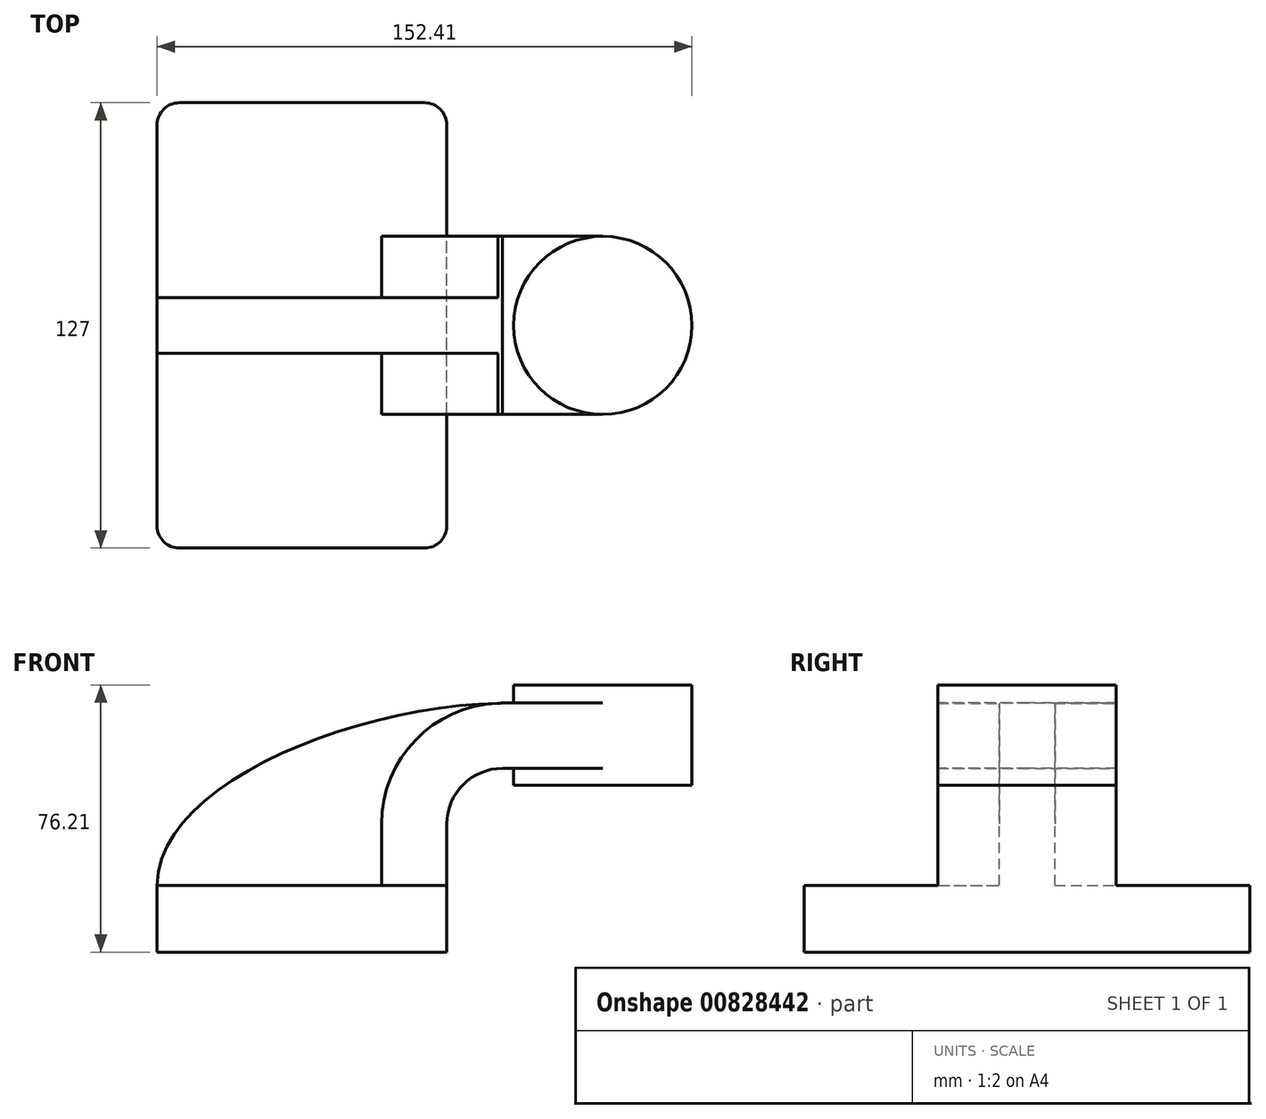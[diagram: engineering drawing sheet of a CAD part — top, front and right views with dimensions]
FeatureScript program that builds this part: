
annotation { "Feature Type Name" : "Feature", "Feature Type Description" : "" }
export const myFeature = defineFeature(function(context is Context, id is Id, definition is map)
    precondition{}
    {
        {
            var Q0;
            Q0=qCreatedBy(makeId("Front.planeOp"),FACE);
            var sketch = newSketch(context, id + "F0", { "sketchPlane" : qUnion([Q0])});
            skLineSegment(sketch, "E0.bottom", {"start": v(-41.28, 9.52) * mm, "end": v(41.28, 9.53) * mm});
            skLineSegment(sketch, "E0.top", {"start": v(-41.28, -9.53) * mm, "end": v(41.28, -9.53) * mm});
            skLineSegment(sketch, "E0.left", {"start": v(-41.28, 9.52) * mm, "end": v(-41.28, -9.53) * mm});
            skLineSegment(sketch, "E0.right", {"start": v(41.28, 9.53) * mm, "end": v(41.28, -9.52) * mm});
            skPoint(sketch, "E0.middle", {"position": v(0, 0) * mm});
            skLineSegment(sketch, "E1.bottom", {"start": v(60.32, 66.67) * mm, "end": v(111.13, 66.67) * mm});
            skLineSegment(sketch, "E1.top", {"start": v(60.32, 38.1) * mm, "end": v(111.13, 38.1) * mm});
            skLineSegment(sketch, "E1.left", {"start": v(60.32, 66.67) * mm, "end": v(60.32, 38.1) * mm});
            skLineSegment(sketch, "E1.right", {"start": v(111.13, 66.67) * mm, "end": v(111.13, 38.1) * mm});
            skPoint(sketch, "E1.middle", {"position": v(85.72, 52.39) * mm});
            skLineSegment(sketch, "E2", {"start": v(41.27, 9.53) * mm, "end": v(41.27, 27) * mm});
            skArc(sketch, "E3", {"start": v(41.27, 27) * mm, "mid": v(45.92, 38.23) * mm, "end": v(57.15, 42.88) * mm});
            skLineSegment(sketch, "E4.0", {"start": v(57.15, 61.48) * mm, "end": v(85.72, 61.48) * mm});
            skArc(sketch, "E4.1", {"start": v(22.67, 27) * mm, "mid": v(32.77, 51.38) * mm, "end": v(57.15, 61.48) * mm});
            skLineSegment(sketch, "E4.2", {"start": v(22.67, 9.53) * mm, "end": v(22.67, 27) * mm});
            skFitSpline(sketch, "E5", {"points": [v(-41.28, 9.52) * mm, v(57.15, 61.48) * mm], "startDerivative": vector(0.65, 87.68) * mm, "endDerivative": vector(125, 1.7) * mm});
            skLineSegment(sketch, "E6", {"start": v(57.15, 42.88) * mm, "end": v(85.72, 42.88) * mm});
            skLineSegment(sketch, "E7", {"start": v(85.72, 38.1) * mm, "end": v(85.72, 66.67) * mm});
            skSolve(sketch);
        }
        {
            var Q0;
            Q0=makeQuery(id+"F0.imprint","IMPRINT",FACE,{"disambiguationData":[TD([[makeQuery(id+"F0.imprint","IMPRINT",EDGE,{"derivedFrom":sQuery(id+"F0.wireOp",EDGE,"E0.top")}),1.0]])]});
            extrude(context, id + "F1", {"entities" : qUnion([Q0]), "endBound" : BoundingType.SYMMETRIC, "depth" : 127 * mm, "offsetDistance" : 25.4 * mm});
        }
        {
            var Q0;
            {var subQ1=sQuery(id+"F0.wireOp",EDGE,"E2");Q0=makeQuery(id+"F0.imprint","IMPRINT",FACE,{"disambiguationData":[TD([[makeQuery(id+"F0.imprint","IMPRINT",EDGE,{"derivedFrom":subQ1}),1.0]])]});}
            var Q1;
            {var subQ0=sQuery(id+"F0.wireOp",EDGE,"E4.0");var subQ1=sQuery(id+"F0.wireOp",EDGE,"E1.left");var subQ2=makeQuery(id+"F0.imprint","INTERSECT",VERTEX,{"derivedFrom":[subQ1,subQ0]});Q1=makeQuery(id+"F0.imprint","IMPRINT",FACE,{"disambiguationData":[TD([[makeQuery(id+"F0.imprint","IMPRINT",EDGE,{"disambiguationData":[TD([[subQ2,-1.0]])],"derivedFrom":subQ1}),1.0]])]});}
            extrude(context, id + "F2", {"entities" : qUnion([Q0, Q1]), "operationType" : NewBodyOperationType.ADD, "endBound" : BoundingType.SYMMETRIC, "depth" : 50.8 * mm, "offsetDistance" : 25.4 * mm});
        }
        {
            var Q0;
            {var subQ3=sQuery(id+"F0.wireOp",EDGE,"E4.2");Q0=makeQuery(id+"F0.imprint","IMPRINT",FACE,{"disambiguationData":[TD([[makeQuery(id+"F0.imprint","IMPRINT",EDGE,{"derivedFrom":subQ3}),1.0]])]});}
            extrude(context, id + "F3", {"entities" : qUnion([Q0]), "operationType" : NewBodyOperationType.ADD, "endBound" : BoundingType.SYMMETRIC, "depth" : 15.88 * mm, "offsetDistance" : 25.4 * mm});
        }
        {
            var Q0;
            {var subQ4=sQuery(id+"F0.wireOp",EDGE,"E1.right");Q0=makeQuery(id+"F0.imprint","IMPRINT",FACE,{"disambiguationData":[TD([[makeQuery(id+"F0.imprint","IMPRINT",EDGE,{"derivedFrom":subQ4}),-1.0]])]});}
            var Q1;
            Q1=sQuery(id+"F0.wireOp",EDGE,"E7");
            revolve(context, id + "F4", {"operationType" : NewBodyOperationType.ADD, "surfaceOperationType" : NewSurfaceOperationType.NEW, "entities" : qUnion([Q0]), "axis" : qUnion([Q1]), "revolveType" : RevolveType.FULL});
        }
        {
            var Q0;
            Q0=makeQuery(id+"F1.opExtrude","CAP_EDGE",EDGE,{"disambiguationData":[OSD([sQuery(id+"F0.wireOp",EDGE,"E0.left")])],"isStart":false});
            var Q1;
            Q1=makeQuery(id+"F1.opExtrude","CAP_EDGE",EDGE,{"disambiguationData":[OSD([sQuery(id+"F0.wireOp",EDGE,"E0.right")])],"isStart":false});
            var Q2;
            Q2=makeQuery(id+"F1.opExtrude","CAP_EDGE",EDGE,{"disambiguationData":[OSD([sQuery(id+"F0.wireOp",EDGE,"E0.right")])],"isStart":true});
            var Q3;
            Q3=makeQuery(id+"F1.opExtrude","CAP_EDGE",EDGE,{"disambiguationData":[OSD([sQuery(id+"F0.wireOp",EDGE,"E0.left")])],"isStart":true});
            fillet(context, id + "F5", {"entities" : qUnion([Q0, Q1, Q2, Q3]), "radius" : 6.35 * mm, "tangentPropagation" : true, "allowEdgeOverflow" : false});
        }
    });
